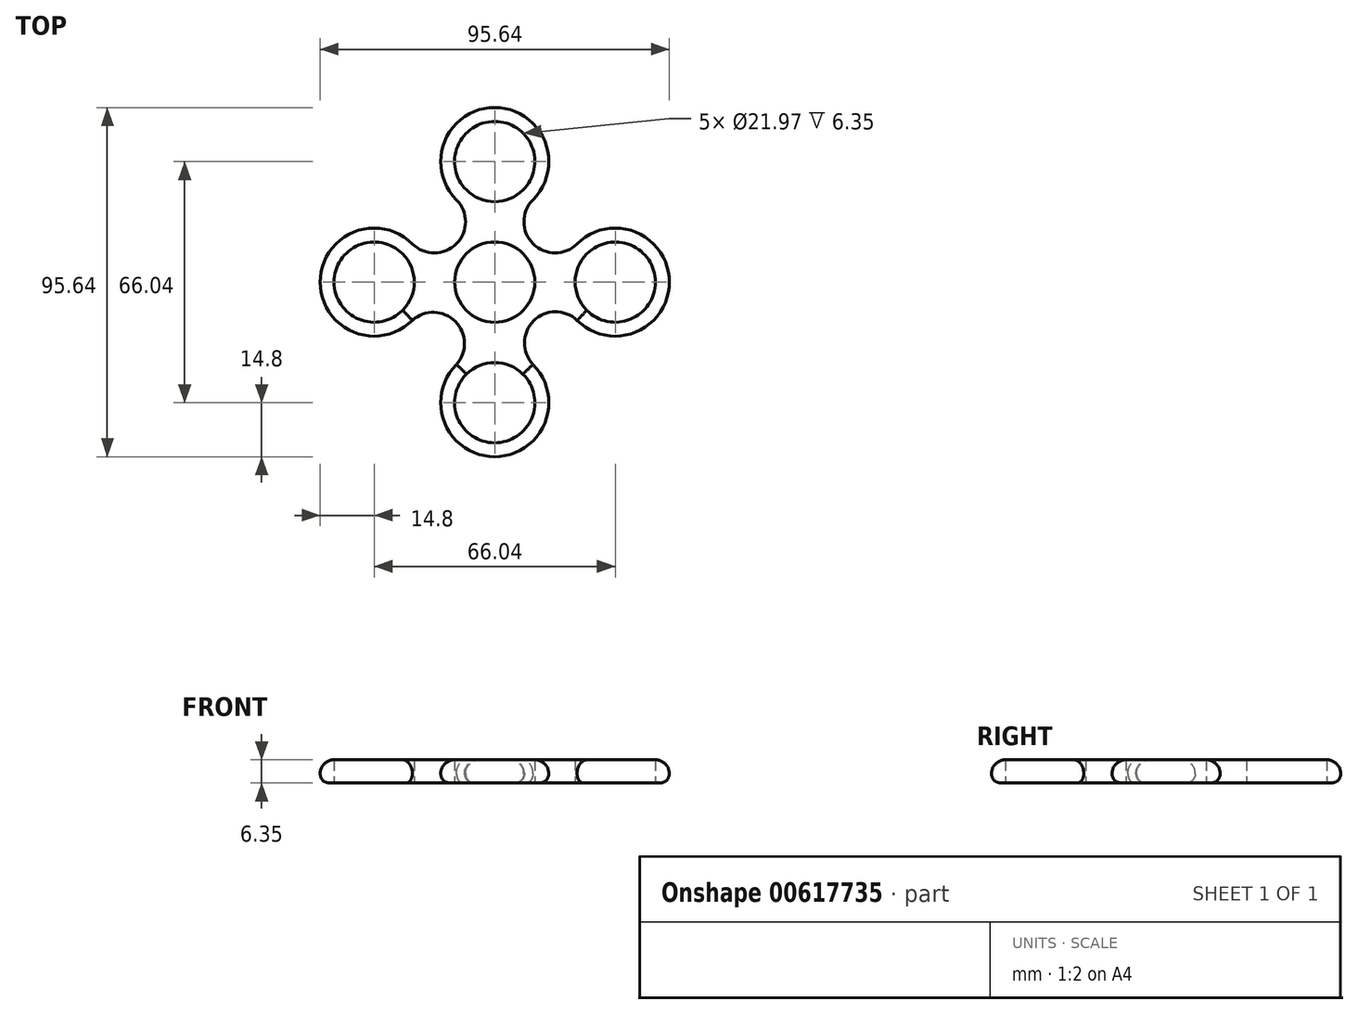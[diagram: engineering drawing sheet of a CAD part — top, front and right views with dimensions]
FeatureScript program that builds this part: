
annotation { "Feature Type Name" : "Feature", "Feature Type Description" : "" }
export const myFeature = defineFeature(function(context is Context, id is Id, definition is map)
    precondition{}
    {
        {
            var Q0;
            Q0=qCreatedBy(makeId("Top.planeOp"),FACE);
            var sketch = newSketch(context, id + "F0", { "sketchPlane" : qUnion([Q0])});
            skCircle(sketch, "E0", {"center": v(0, 0) * mm, "radius": 10.99 * mm});
            skCircle(sketch, "E1", {"center": v(0, 0) * mm, "radius": 14.8 * mm});
            skLineSegment(sketch, "E2", {"start": v(0, 0) * mm, "end": v(0, 33.02) * mm});
            skCircle(sketch, "E3", {"center": v(0, 33.02) * mm, "radius": 10.99 * mm});
            skCircle(sketch, "E4", {"center": v(0, 33.02) * mm, "radius": 14.8 * mm});
            skCircle(sketch, "E5.1.0", {"center": v(-33.02, 0) * mm, "radius": 14.8 * mm});
            skCircle(sketch, "E5.1.1", {"center": v(-33.02, 0) * mm, "radius": 10.99 * mm});
            skLineSegment(sketch, "E5.1.2", {"start": v(0, 0) * mm, "end": v(-33.02, 0) * mm});
            skCircle(sketch, "E5.2.0", {"center": v(0, -33.02) * mm, "radius": 14.8 * mm});
            skCircle(sketch, "E5.2.1", {"center": v(0, -33.02) * mm, "radius": 10.99 * mm});
            skLineSegment(sketch, "E5.2.2", {"start": v(0, 0) * mm, "end": v(0, -33.02) * mm});
            skCircle(sketch, "E5.3.0", {"center": v(33.02, 0) * mm, "radius": 14.8 * mm});
            skCircle(sketch, "E5.3.1", {"center": v(33.02, 0) * mm, "radius": 10.99 * mm});
            skLineSegment(sketch, "E5.3.2", {"start": v(0, 0) * mm, "end": v(33.02, 0) * mm});
            skPoint(sketch, "E6", {"position": v(-10.46, 22.56) * mm});
            skPoint(sketch, "E7", {"position": v(-22.56, 10.46) * mm});
            skPoint(sketch, "E8", {"position": v(-22.56, -10.46) * mm});
            skPoint(sketch, "E9", {"position": v(-10.46, -22.56) * mm});
            skPoint(sketch, "E10", {"position": v(10.46, -22.56) * mm});
            skPoint(sketch, "E11", {"position": v(22.56, -10.46) * mm});
            skPoint(sketch, "E12", {"position": v(22.56, 10.46) * mm});
            skPoint(sketch, "E13", {"position": v(10.46, 22.56) * mm});
            skArc(sketch, "E14", {"start": v(-22.56, 10.46) * mm, "mid": v(-10.5, 10.5) * mm, "end": v(-10.46, 22.56) * mm});
            skArc(sketch, "E15", {"start": v(10.46, 22.56) * mm, "mid": v(10.5, 10.5) * mm, "end": v(22.56, 10.46) * mm});
            skArc(sketch, "E16", {"start": v(22.56, -10.46) * mm, "mid": v(10.63, -10.63) * mm, "end": v(10.46, -22.56) * mm});
            skArc(sketch, "E17", {"start": v(-10.46, -22.56) * mm, "mid": v(-10.79, -10.79) * mm, "end": v(-22.56, -10.46) * mm});
            skSolve(sketch);
        }
        {
            var Q0;
            Q0=makeQuery(id+"F0.imprint","IMPRINT",FACE,{"disambiguationData":[TD([[makeQuery(id+"F0.imprint","IMPRINT",EDGE,{"derivedFrom":sQuery(id+"F0.wireOp",EDGE,"E5.1.1")}),-1.0]])]});
            var Q1;
            {var subQ0=sQuery(id+"F0.wireOp",EDGE,"E14");Q1=makeQuery(id+"F0.imprint","IMPRINT",FACE,{"disambiguationData":[TD([[makeQuery(id+"F0.imprint","IMPRINT",EDGE,{"derivedFrom":subQ0}),-1.0]])]});}
            var Q2;
            {var subQ0=sQuery(id+"F0.wireOp",EDGE,"E17");Q2=makeQuery(id+"F0.imprint","IMPRINT",FACE,{"disambiguationData":[TD([[makeQuery(id+"F0.imprint","IMPRINT",EDGE,{"derivedFrom":subQ0}),-1.0]])]});}
            var Q3;
            {var subQ0=sQuery(id+"F0.wireOp",EDGE,"E5.1.2");var subQ1=sQuery(id+"F0.wireOp",EDGE,"E0");var subQ2=makeQuery(id+"F0.imprint","INTERSECT",VERTEX,{"derivedFrom":[subQ1,subQ0]});Q3=makeQuery(id+"F0.imprint","IMPRINT",FACE,{"disambiguationData":[TD([[makeQuery(id+"F0.imprint","IMPRINT",EDGE,{"disambiguationData":[TD([[subQ2,-1.0]])],"derivedFrom":subQ1}),-1.0]])]});}
            var Q4;
            {var subQ0=sQuery(id+"F0.wireOp",EDGE,"E5.3.2");var subQ1=sQuery(id+"F0.wireOp",EDGE,"E0");var subQ2=makeQuery(id+"F0.imprint","INTERSECT",VERTEX,{"derivedFrom":[subQ1,subQ0]});Q4=makeQuery(id+"F0.imprint","IMPRINT",FACE,{"disambiguationData":[TD([[makeQuery(id+"F0.imprint","IMPRINT",EDGE,{"disambiguationData":[TD([[subQ2,1.0]])],"derivedFrom":subQ1}),-1.0]])]});}
            var Q5;
            {var subQ0=sQuery(id+"F0.wireOp",EDGE,"E16");Q5=makeQuery(id+"F0.imprint","IMPRINT",FACE,{"disambiguationData":[TD([[makeQuery(id+"F0.imprint","IMPRINT",EDGE,{"derivedFrom":subQ0}),-1.0]])]});}
            var Q6;
            {var subQ0=sQuery(id+"F0.wireOp",EDGE,"E2");var subQ1=sQuery(id+"F0.wireOp",EDGE,"E0");var subQ2=makeQuery(id+"F0.imprint","INTERSECT",VERTEX,{"derivedFrom":[subQ1,subQ0]});Q6=makeQuery(id+"F0.imprint","IMPRINT",FACE,{"disambiguationData":[TD([[makeQuery(id+"F0.imprint","IMPRINT",EDGE,{"disambiguationData":[TD([[subQ2,1.0]])],"derivedFrom":subQ1}),-1.0]])]});}
            var Q7;
            {var subQ0=sQuery(id+"F0.wireOp",EDGE,"E15");Q7=makeQuery(id+"F0.imprint","IMPRINT",FACE,{"disambiguationData":[TD([[makeQuery(id+"F0.imprint","IMPRINT",EDGE,{"derivedFrom":subQ0}),-1.0]])]});}
            var Q8;
            {var subQ0=sQuery(id+"F0.wireOp",EDGE,"E2");var subQ1=sQuery(id+"F0.wireOp",EDGE,"E0");var subQ2=makeQuery(id+"F0.imprint","INTERSECT",VERTEX,{"derivedFrom":[subQ1,subQ0]});Q8=makeQuery(id+"F0.imprint","IMPRINT",FACE,{"disambiguationData":[TD([[makeQuery(id+"F0.imprint","IMPRINT",EDGE,{"disambiguationData":[TD([[subQ2,-1.0]])],"derivedFrom":subQ1}),-1.0]])]});}
            var Q9;
            Q9=makeQuery(id+"F0.imprint","IMPRINT",FACE,{"disambiguationData":[TD([[makeQuery(id+"F0.imprint","IMPRINT",EDGE,{"derivedFrom":sQuery(id+"F0.wireOp",EDGE,"E3")}),-1.0]])]});
            var Q10;
            Q10=makeQuery(id+"F0.imprint","IMPRINT",FACE,{"disambiguationData":[TD([[makeQuery(id+"F0.imprint","IMPRINT",EDGE,{"derivedFrom":sQuery(id+"F0.wireOp",EDGE,"E5.3.1")}),-1.0]])]});
            var Q11;
            Q11=makeQuery(id+"F0.imprint","IMPRINT",FACE,{"disambiguationData":[TD([[makeQuery(id+"F0.imprint","IMPRINT",EDGE,{"derivedFrom":sQuery(id+"F0.wireOp",EDGE,"E5.2.1")}),-1.0]])]});
            extrude(context, id + "F1", {"entities" : qUnion([Q0, Q1, Q2, Q3, Q4, Q5, Q6, Q7, Q8, Q9, Q10, Q11]), "depth" : 6.35 * mm, "offsetDistance" : 25.4 * mm});
        }
        {
            var Q0;
            Q0=makeQuery(id+"F1.opExtrude","CAP_EDGE",EDGE,{"disambiguationData":[OSD([sQuery(id+"F0.wireOp",EDGE,"E5.1.0")])],"isStart":false});
            var Q1;
            Q1=makeQuery(id+"F1.opExtrude","CAP_EDGE",EDGE,{"disambiguationData":[OSD([sQuery(id+"F0.wireOp",EDGE,"E14")])],"isStart":false});
            var Q2;
            Q2=makeQuery(id+"F1.opExtrude","CAP_EDGE",EDGE,{"disambiguationData":[OSD([sQuery(id+"F0.wireOp",EDGE,"E4")])],"isStart":false});
            var Q3;
            Q3=makeQuery(id+"F1.opExtrude","CAP_EDGE",EDGE,{"disambiguationData":[OSD([sQuery(id+"F0.wireOp",EDGE,"E17")])],"isStart":false});
            var Q4;
            Q4=makeQuery(id+"F1.opExtrude","CAP_EDGE",EDGE,{"disambiguationData":[OSD([sQuery(id+"F0.wireOp",EDGE,"E5.2.0")])],"isStart":false});
            var Q5;
            Q5=makeQuery(id+"F1.opExtrude","CAP_EDGE",EDGE,{"disambiguationData":[OSD([sQuery(id+"F0.wireOp",EDGE,"E16")])],"isStart":false});
            var Q6;
            Q6=makeQuery(id+"F1.opExtrude","CAP_EDGE",EDGE,{"disambiguationData":[OSD([sQuery(id+"F0.wireOp",EDGE,"E5.3.0")])],"isStart":false});
            var Q7;
            Q7=makeQuery(id+"F1.opExtrude","CAP_EDGE",EDGE,{"disambiguationData":[OSD([sQuery(id+"F0.wireOp",EDGE,"E15")])],"isStart":false});
            fillet(context, id + "F2", {"entities" : qUnion([Q0, Q1, Q2, Q3, Q4, Q5, Q6, Q7]), "radius" : 3.8 * mm, "tangentPropagation" : true, "allowEdgeOverflow" : false});
        }
        {
            var Q0;
            Q0=makeQuery(id+"F1.opExtrude","CAP_EDGE",EDGE,{"disambiguationData":[OSD([sQuery(id+"F0.wireOp",EDGE,"E5.2.0")])],"isStart":true});
            var Q1;
            Q1=makeQuery(id+"F1.opExtrude","CAP_EDGE",EDGE,{"disambiguationData":[OSD([sQuery(id+"F0.wireOp",EDGE,"E17")])],"isStart":true});
            var Q2;
            Q2=makeQuery(id+"F1.opExtrude","CAP_EDGE",EDGE,{"disambiguationData":[OSD([sQuery(id+"F0.wireOp",EDGE,"E5.1.0")])],"isStart":true});
            var Q3;
            Q3=makeQuery(id+"F1.opExtrude","CAP_EDGE",EDGE,{"disambiguationData":[OSD([sQuery(id+"F0.wireOp",EDGE,"E14")])],"isStart":true});
            var Q4;
            Q4=makeQuery(id+"F1.opExtrude","CAP_EDGE",EDGE,{"disambiguationData":[OSD([sQuery(id+"F0.wireOp",EDGE,"E5.3.0")])],"isStart":true});
            var Q5;
            Q5=makeQuery(id+"F1.opExtrude","CAP_EDGE",EDGE,{"disambiguationData":[OSD([sQuery(id+"F0.wireOp",EDGE,"E16")])],"isStart":true});
            var Q6;
            Q6=makeQuery(id+"F1.opExtrude","CAP_EDGE",EDGE,{"disambiguationData":[OSD([sQuery(id+"F0.wireOp",EDGE,"E4")])],"isStart":true});
            fillet(context, id + "F3", {"entities" : qUnion([Q0, Q1, Q2, Q3, Q4, Q5, Q6]), "radius" : 2.54 * mm, "tangentPropagation" : true, "allowEdgeOverflow" : false});
        }
    });
